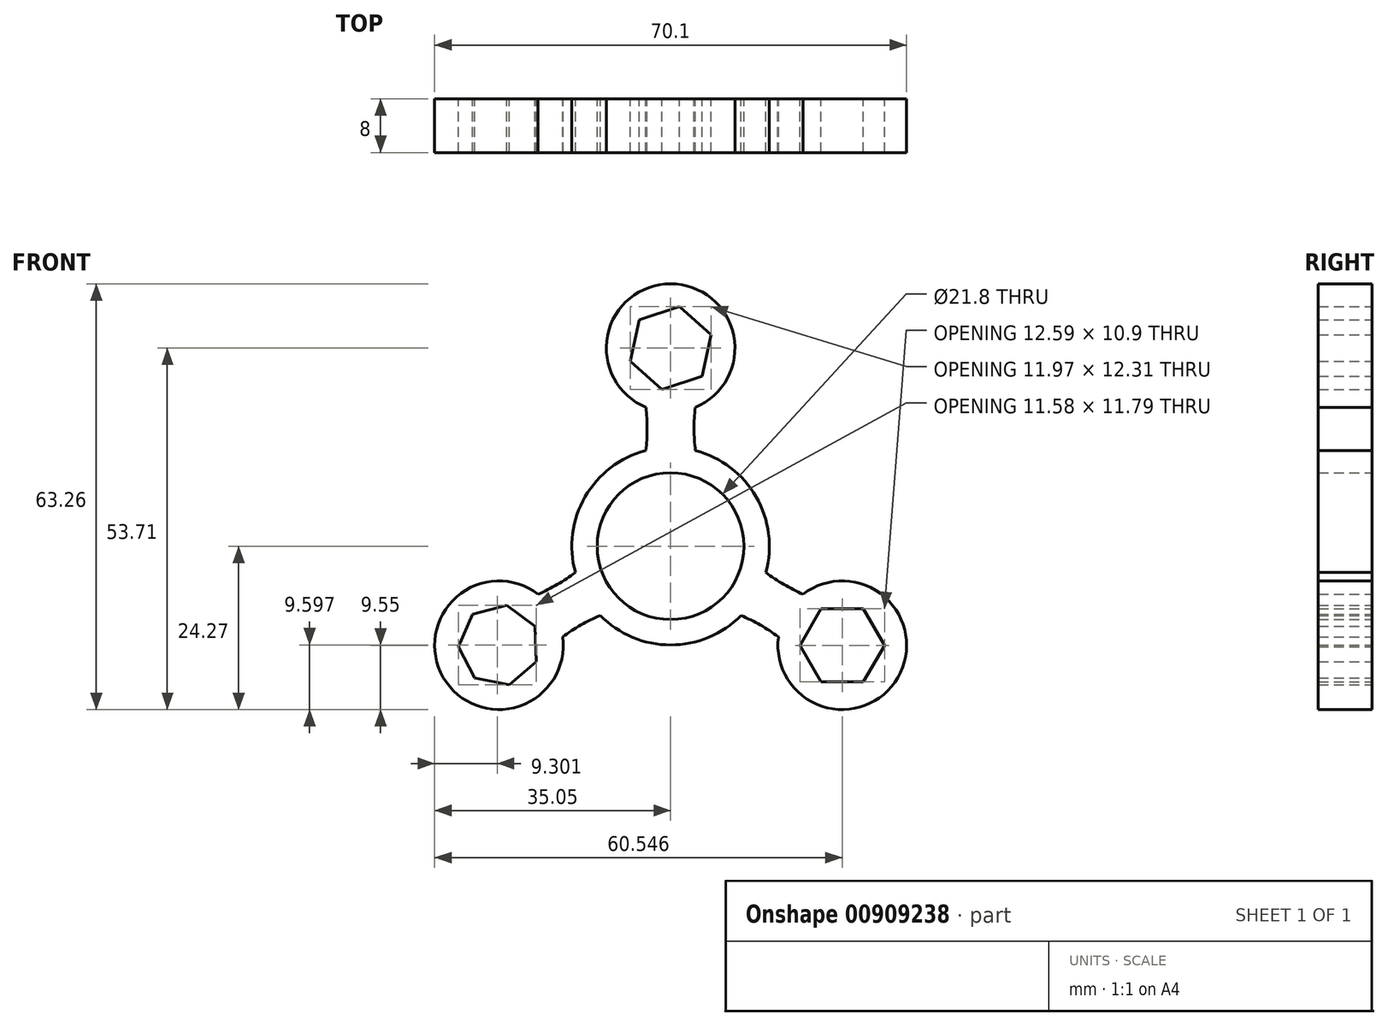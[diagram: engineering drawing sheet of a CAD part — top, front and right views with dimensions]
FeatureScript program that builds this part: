
annotation { "Feature Type Name" : "Feature", "Feature Type Description" : "" }
export const myFeature = defineFeature(function(context is Context, id is Id, definition is map)
    precondition{}
    {
        {
            var Q0;
            Q0=qCreatedBy(makeId("Front.planeOp"),FACE);
            var sketch = newSketch(context, id + "F0", { "sketchPlane" : qUnion([Q0])});
            skCircle(sketch, "E0", {"center": v(0, 0) * mm, "radius": 6.16 * mm});
            skLineSegment(sketch, "E1", {"start": v(-3.67, 20.62) * mm, "end": v(-3.67, 20.75) * mm});
            skLineSegment(sketch, "E2.MirrorCS", {"start": v(3.67, 20.62) * mm, "end": v(3.67, 20.75) * mm});
            skArc(sketch, "E3", {"start": v(3.66, 20.61) * mm, "mid": v(0, 39) * mm, "end": v(-3.66, 20.61) * mm});
            skLineSegment(sketch, "E4.1.0", {"start": v(-16.02, -13.5) * mm, "end": v(-16.13, -13.55) * mm});
            skLineSegment(sketch, "E4.1.1", {"start": v(-19.7, -7.13) * mm, "end": v(-19.8, -7.2) * mm});
            skArc(sketch, "E4.1.2", {"start": v(-19.68, -7.14) * mm, "mid": v(-33.77, -19.5) * mm, "end": v(-16.02, -13.47) * mm});
            skLineSegment(sketch, "E4.2.0", {"start": v(19.7, -7.13) * mm, "end": v(19.8, -7.2) * mm});
            skLineSegment(sketch, "E4.2.1", {"start": v(16.02, -13.5) * mm, "end": v(16.13, -13.55) * mm});
            skArc(sketch, "E4.2.2", {"start": v(16.02, -13.47) * mm, "mid": v(33.77, -19.5) * mm, "end": v(19.68, -7.14) * mm});
            skCircle(sketch, "E5.cCircle", {"center": v(-25.5, -14.72) * mm, "radius": 5.45 * mm, "construction": true});
            skLineSegment(sketch, "E5.0", {"start": v(-29.1, -19.58) * mm, "end": v(-31.54, -14.93) * mm});
            skLineSegment(sketch, "E5.1", {"start": v(-31.54, -14.93) * mm, "end": v(-29.43, -10.13) * mm});
            skLineSegment(sketch, "E5.2", {"start": v(-29.43, -10.13) * mm, "end": v(-24.36, -8.78) * mm});
            skLineSegment(sketch, "E5.3", {"start": v(-24.36, -8.78) * mm, "end": v(-20.14, -11.9) * mm});
            skLineSegment(sketch, "E5.4", {"start": v(-20.14, -11.9) * mm, "end": v(-19.96, -17.15) * mm});
            skLineSegment(sketch, "E5.5", {"start": v(-19.96, -17.15) * mm, "end": v(-23.94, -20.57) * mm});
            skLineSegment(sketch, "E5.6", {"start": v(-23.94, -20.57) * mm, "end": v(-29.1, -19.58) * mm});
            skPoint(sketch, "E5.0.midPoint", {"position": v(-30.32, -17.26) * mm});
            skCircle(sketch, "E6.cCircle", {"center": v(0, 29.44) * mm, "radius": 5.45 * mm, "construction": true});
            skLineSegment(sketch, "E6.0", {"start": v(-1.3, 23.28) * mm, "end": v(-5.98, 27.49) * mm});
            skLineSegment(sketch, "E6.1", {"start": v(-5.98, 27.49) * mm, "end": v(-4.68, 33.65) * mm});
            skLineSegment(sketch, "E6.2", {"start": v(-4.68, 33.65) * mm, "end": v(1.3, 35.6) * mm});
            skLineSegment(sketch, "E6.3", {"start": v(1.3, 35.6) * mm, "end": v(5.98, 31.4) * mm});
            skLineSegment(sketch, "E6.4", {"start": v(5.98, 31.4) * mm, "end": v(4.68, 25.23) * mm});
            skLineSegment(sketch, "E6.5", {"start": v(4.68, 25.23) * mm, "end": v(-1.3, 23.28) * mm});
            skPoint(sketch, "E6.0.midPoint", {"position": v(-3.64, 25.39) * mm});
            skCircle(sketch, "E7.cCircle", {"center": v(25.5, -14.72) * mm, "radius": 5.45 * mm, "construction": true});
            skLineSegment(sketch, "E7.0", {"start": v(28.64, -20.17) * mm, "end": v(22.35, -20.17) * mm});
            skLineSegment(sketch, "E7.1", {"start": v(22.35, -20.17) * mm, "end": v(19.2, -14.72) * mm});
            skLineSegment(sketch, "E7.2", {"start": v(19.2, -14.72) * mm, "end": v(22.35, -9.27) * mm});
            skLineSegment(sketch, "E7.3", {"start": v(22.35, -9.27) * mm, "end": v(28.64, -9.27) * mm});
            skLineSegment(sketch, "E7.4", {"start": v(28.64, -9.27) * mm, "end": v(31.79, -14.72) * mm});
            skLineSegment(sketch, "E7.5", {"start": v(31.79, -14.72) * mm, "end": v(28.64, -20.17) * mm});
            skPoint(sketch, "E7.0.midPoint", {"position": v(25.5, -20.17) * mm});
            skCircle(sketch, "E8", {"center": v(0, 0) * mm, "radius": 3.67 * mm});
            skArc(sketch, "E9", {"start": v(3.67, 20.75) * mm, "mid": v(3.48, 17.47) * mm, "end": v(3.7, 14.2) * mm});
            skArc(sketch, "E10.1.0", {"start": v(-19.8, -7.2) * mm, "mid": v(-16.87, -5.72) * mm, "end": v(-14.14, -3.9) * mm});
            skArc(sketch, "E10.2.0", {"start": v(16.13, -13.55) * mm, "mid": v(13.4, -11.75) * mm, "end": v(10.45, -10.3) * mm});
            skPoint(sketch, "E11.orphan", {"position": v(-3.67, 4.94) * mm});
            skPoint(sketch, "E12.orphan", {"position": v(3.67, 4.94) * mm});
            skArc(sketch, "E13", {"start": v(10.86, -0.96) * mm, "mid": v(-9.44, 5.45) * mm, "end": v(6.26, -8.92) * mm});
            skArc(sketch, "E14", {"start": v(-3.7, 14.2) * mm, "mid": v(-12.7, 7.34) * mm, "end": v(-14.14, -3.9) * mm});
            skArc(sketch, "E15.trimOffspring", {"start": v(-3.7, 14.2) * mm, "mid": v(-3.48, 17.47) * mm, "end": v(-3.67, 20.75) * mm});
            skArc(sketch, "E16.trimOffspring", {"start": v(14.14, -3.9) * mm, "mid": v(16.87, -5.72) * mm, "end": v(19.8, -7.2) * mm});
            skArc(sketch, "E17.trimOffspring", {"start": v(-10.45, -10.3) * mm, "mid": v(-13.4, -11.75) * mm, "end": v(-16.13, -13.55) * mm});
            skArc(sketch, "E18.trimOffspring", {"start": v(14.14, -3.9) * mm, "mid": v(12.7, 7.34) * mm, "end": v(3.7, 14.2) * mm});
            skArc(sketch, "E19.trimOffspring", {"start": v(-10.45, -10.3) * mm, "mid": v(0, -14.67) * mm, "end": v(10.45, -10.3) * mm});
            skCircle(sketch, "E20", {"center": v(0, 0) * mm, "radius": 10.9 * mm});
            skSolve(sketch);
        }
        {
            var Q0;
            Q0 = qSketchRegion(id + "F0", true);
            extrude(context, id + "F1", {"entities" : qUnion([Q0]), "depth" : 8 * mm, "offsetDistance" : 25 * mm});
        }
    });
